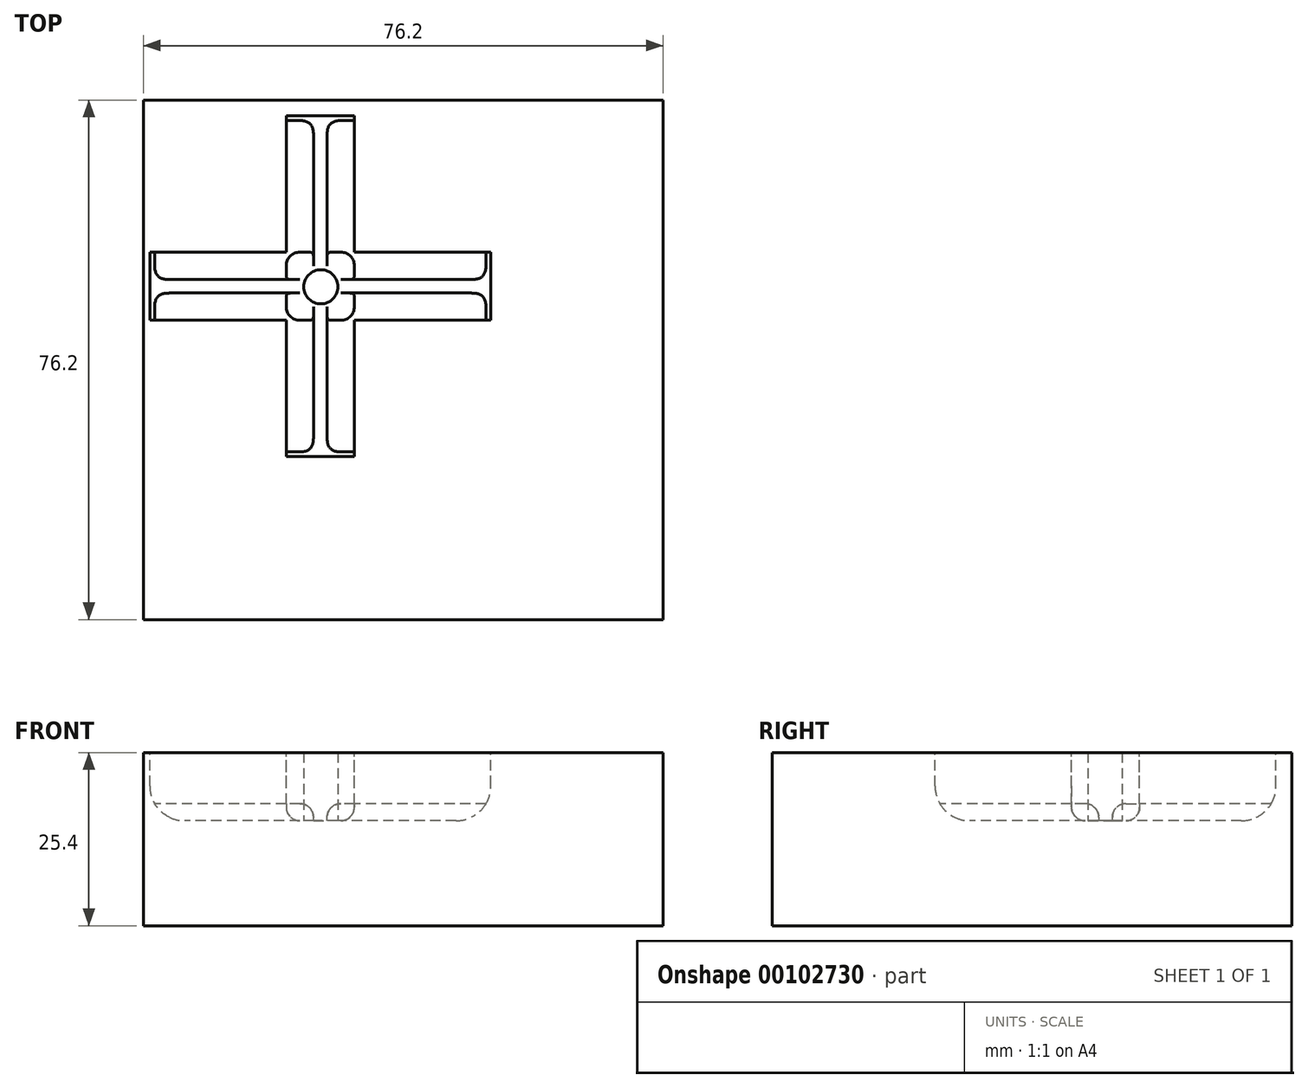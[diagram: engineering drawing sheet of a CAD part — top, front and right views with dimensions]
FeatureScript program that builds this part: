
annotation { "Feature Type Name" : "Feature", "Feature Type Description" : "" }
export const myFeature = defineFeature(function(context is Context, id is Id, definition is map)
    precondition{}
    {
        {
            var Q0;
            Q0=qCreatedBy(makeId("Top.planeOp"),FACE);
            var sketch = newSketch(context, id + "F0", { "sketchPlane" : qUnion([Q0])});
            skLineSegment(sketch, "E0.bottom", {"start": v(0, 0) * mm, "end": v(50.8, 0) * mm});
            skLineSegment(sketch, "E0.top", {"start": v(0, -50.8) * mm, "end": v(50.8, -50.8) * mm});
            skLineSegment(sketch, "E0.left", {"start": v(0, 0) * mm, "end": v(0, -50.8) * mm});
            skLineSegment(sketch, "E0.right", {"start": v(50.8, 0) * mm, "end": v(50.8, -50.8) * mm});
            skSolve(sketch);
        }
        {
            var Q0;
            Q0=makeQuery(id+"F0.imprint","IMPRINT",FACE,{"disambiguationData":[TD([[makeQuery(id+"F0.imprint","IMPRINT",EDGE,{"derivedFrom":sQuery(id+"F0.wireOp",EDGE,"E0.bottom")}),-1.0]])]});
            extrude(context, id + "F1", {"entities" : qUnion([Q0]), "depth" : 25.4 * mm});
        }
        {
            var Q0;
            Q0=makeQuery(id+"F1.opExtrude","SWEPT_FACE",FACE,{"disambiguationData":[OSD([sQuery(id+"F0.wireOp",EDGE,"E0.top")])]});
            extrude(context, id + "F2", {"entities" : qUnion([Q0]), "operationType" : NewBodyOperationType.ADD, "depth" : 25.4 * mm});
        }
        {
            var Q0;
            {var subQ0=sQuery(id+"F0.wireOp",EDGE,"E0.top");Q0=makeQuery(id+"F2.boolean.opBoolean","MERGE",FACE,{"derivedFrom":[makeQuery(id+"F1.opExtrude","CAP_FACE",FACE,{"disambiguationData":[OSD([sQuery(id+"F0.wireOp",EDGE,"E0.bottom"),subQ0,sQuery(id+"F0.wireOp",EDGE,"E0.left"),sQuery(id+"F0.wireOp",EDGE,"E0.right")])],"isStart":false}),makeQuery(id+"F2.opExtrude","SWEPT_FACE",FACE,{"disambiguationData":[OSD([subQ0]),TDD([makeQuery(id+"F1.opExtrude","CAP_EDGE",EDGE,{"disambiguationData":[OSD([subQ0])],"isStart":false})])]})]});}
            var sketch = newSketch(context, id + "F3", { "sketchPlane" : qUnion([Q0])});
            skPoint(sketch, "E1.startSnap0", {"position": v(25.4, 0) * mm});
            skLineSegment(sketch, "E2.0", {"start": v(20.93, -12.32) * mm, "end": v(20.93, -22.32) * mm});
            skLineSegment(sketch, "E3.0", {"start": v(30.93, -12.32) * mm, "end": v(30.93, -22.32) * mm});
            skLineSegment(sketch, "E4.0", {"start": v(40.93, -22.32) * mm, "end": v(30.93, -22.32) * mm});
            skLineSegment(sketch, "E5.0", {"start": v(20.93, -22.32) * mm, "end": v(10.93, -22.32) * mm});
            skLineSegment(sketch, "E6.0", {"start": v(20.93, -32.32) * mm, "end": v(10.93, -32.32) * mm});
            skLineSegment(sketch, "E7.0", {"start": v(40.93, -32.32) * mm, "end": v(30.93, -32.32) * mm});
            skLineSegment(sketch, "E8", {"start": v(10.93, -22.32) * mm, "end": v(10.93, -32.32) * mm});
            skLineSegment(sketch, "E9", {"start": v(40.93, -22.32) * mm, "end": v(40.93, -32.32) * mm});
            skLineSegment(sketch, "E10", {"start": v(30.93, -12.32) * mm, "end": v(20.93, -12.32) * mm});
            skLineSegment(sketch, "E11", {"start": v(20.93, -42.32) * mm, "end": v(30.93, -42.32) * mm});
            skPoint(sketch, "E12.orphan", {"position": v(25.4, -22.99) * mm});
            skPoint(sketch, "E13.orphan", {"position": v(25.93, -42.32) * mm});
            skLineSegment(sketch, "E14.trimOffspring", {"start": v(30.93, -32.32) * mm, "end": v(30.93, -42.32) * mm});
            skLineSegment(sketch, "E15.trimOffspring", {"start": v(20.93, -32.32) * mm, "end": v(20.93, -42.32) * mm});
            skSolve(sketch);
        }
        {
            var Q0;
            Q0=makeQuery(id+"F3.imprint","IMPRINT",FACE,{"disambiguationData":[TD([[makeQuery(id+"F3.imprint","IMPRINT",EDGE,{"derivedFrom":sQuery(id+"F3.wireOp",EDGE,"E2.0")}),1.0]])]});
            extrude(context, id + "F4", {"entities" : qUnion([Q0]), "operationType" : NewBodyOperationType.REMOVE, "oppositeDirection" : true, "depth" : 10 * mm});
        }
        {
            var Q0;
            Q0=makeQuery(id+"F4.boolean.opBoolean","COPY",FACE,{"derivedFrom":makeQuery(id+"F4.opExtrude","SWEPT_FACE",FACE,{"disambiguationData":[OSD([sQuery(id+"F3.wireOp",EDGE,"E8")])]})});
            extrude(context, id + "F5", {"entities" : qUnion([Q0]), "operationType" : NewBodyOperationType.REMOVE, "oppositeDirection" : true, "depth" : 10 * mm});
        }
        {
            var Q0;
            Q0=makeQuery(id+"F4.boolean.opBoolean","COPY",FACE,{"derivedFrom":makeQuery(id+"F4.opExtrude","SWEPT_FACE",FACE,{"disambiguationData":[OSD([sQuery(id+"F3.wireOp",EDGE,"E10")])]})});
            extrude(context, id + "F6", {"entities" : qUnion([Q0]), "operationType" : NewBodyOperationType.REMOVE, "oppositeDirection" : true, "depth" : 10 * mm});
        }
        {
            var Q0;
            {var subQ0=sQuery(id+"F0.wireOp",EDGE,"E0.right");Q0=makeQuery(id+"F2.boolean.opBoolean","MERGE",FACE,{"derivedFrom":[makeQuery(id+"F1.opExtrude","SWEPT_FACE",FACE,{"disambiguationData":[OSD([subQ0])]}),makeQuery(id+"F2.opExtrude","SWEPT_FACE",FACE,{"disambiguationData":[OSD([sQuery(id+"F0.wireOp",EDGE,"E0.top"),subQ0])]})]});}
            extrude(context, id + "F7", {"entities" : qUnion([Q0]), "operationType" : NewBodyOperationType.ADD, "depth" : 25.4 * mm});
        }
        {
            var Q0;
            Q0=makeQuery(id+"F4.boolean.opBoolean","COPY",FACE,{"derivedFrom":makeQuery(id+"F4.opExtrude","SWEPT_FACE",FACE,{"disambiguationData":[OSD([sQuery(id+"F3.wireOp",EDGE,"E9")])]})});
            extrude(context, id + "F8", {"entities" : qUnion([Q0]), "operationType" : NewBodyOperationType.REMOVE, "oppositeDirection" : true, "depth" : 10 * mm});
        }
        {
            var Q0;
            Q0=makeQuery(id+"F4.boolean.opBoolean","COPY",FACE,{"derivedFrom":makeQuery(id+"F4.opExtrude","SWEPT_FACE",FACE,{"disambiguationData":[OSD([sQuery(id+"F3.wireOp",EDGE,"E11")])]})});
            extrude(context, id + "F9", {"entities" : qUnion([Q0]), "operationType" : NewBodyOperationType.REMOVE, "oppositeDirection" : true, "depth" : 10 * mm});
        }
        {
            var Q0;
            {var subQ0=sQuery(id+"F3.wireOp",EDGE,"E11");var subQ1=sQuery(id+"F3.wireOp",EDGE,"E9");var subQ2=sQuery(id+"F3.wireOp",EDGE,"E10");var subQ3=sQuery(id+"F3.wireOp",EDGE,"E8");Q0=makeQuery(id+"F9.boolean.opBoolean","MERGE",FACE,{"derivedFrom":[makeQuery(id+"F8.boolean.opBoolean","MERGE",FACE,{"derivedFrom":[makeQuery(id+"F6.boolean.opBoolean","MERGE",FACE,{"derivedFrom":[makeQuery(id+"F5.boolean.opBoolean","MERGE",FACE,{"derivedFrom":[makeQuery(id+"F4.boolean.opBoolean","COPY",FACE,{"derivedFrom":makeQuery(id+"F4.opExtrude","CAP_FACE",FACE,{"disambiguationData":[OSD([sQuery(id+"F3.wireOp",EDGE,"E2.0"),sQuery(id+"F3.wireOp",EDGE,"E3.0"),sQuery(id+"F3.wireOp",EDGE,"E4.0"),sQuery(id+"F3.wireOp",EDGE,"E5.0"),sQuery(id+"F3.wireOp",EDGE,"E6.0"),sQuery(id+"F3.wireOp",EDGE,"E7.0"),subQ3,subQ1,subQ2,subQ0,sQuery(id+"F3.wireOp",EDGE,"E14.trimOffspring"),sQuery(id+"F3.wireOp",EDGE,"E15.trimOffspring")])],"isStart":false})}),makeQuery(id+"F5.opExtrude","SWEPT_FACE",FACE,{"disambiguationData":[OSD([subQ3]),TDD([makeQuery(id+"F4.boolean.opBoolean","COPY",EDGE,{"derivedFrom":makeQuery(id+"F4.opExtrude","CAP_EDGE",EDGE,{"disambiguationData":[OSD([subQ3])],"isStart":false})})])]})]}),makeQuery(id+"F6.opExtrude","SWEPT_FACE",FACE,{"disambiguationData":[OSD([subQ2]),TDD([makeQuery(id+"F4.boolean.opBoolean","COPY",EDGE,{"derivedFrom":makeQuery(id+"F4.opExtrude","CAP_EDGE",EDGE,{"disambiguationData":[OSD([subQ2])],"isStart":false})})])]})]}),makeQuery(id+"F8.opExtrude","SWEPT_FACE",FACE,{"disambiguationData":[OSD([subQ1]),TDD([makeQuery(id+"F4.boolean.opBoolean","COPY",EDGE,{"derivedFrom":makeQuery(id+"F4.opExtrude","CAP_EDGE",EDGE,{"disambiguationData":[OSD([subQ1])],"isStart":false})})])]})]}),makeQuery(id+"F9.opExtrude","SWEPT_FACE",FACE,{"disambiguationData":[OSD([subQ0]),TDD([makeQuery(id+"F4.boolean.opBoolean","COPY",EDGE,{"derivedFrom":makeQuery(id+"F4.opExtrude","CAP_EDGE",EDGE,{"disambiguationData":[OSD([subQ0])],"isStart":false})})])]})]});}
            var sketch = newSketch(context, id + "F10", { "sketchPlane" : qUnion([Q0])});
            skCircle(sketch, "E16", {"center": v(26.01, -27.4) * mm, "radius": 2.5 * mm});
            skSolve(sketch);
        }
        {
            var Q0;
            Q0=makeQuery(id+"F10.imprint","IMPRINT",FACE,{"disambiguationData":[TD([[makeQuery(id+"F10.imprint","IMPRINT",EDGE,{"derivedFrom":sQuery(id+"F10.wireOp",EDGE,"E16")}),1.0]])]});
            extrude(context, id + "F11", {"entities" : qUnion([Q0]), "operationType" : NewBodyOperationType.ADD, "depth" : 10 * mm});
        }
        {
            var Q0;
            {var subQ0=sQuery(id+"F3.wireOp",EDGE,"E11");var subQ1=sQuery(id+"F3.wireOp",EDGE,"E9");var subQ2=sQuery(id+"F3.wireOp",EDGE,"E10");var subQ3=sQuery(id+"F3.wireOp",EDGE,"E8");Q0=makeQuery(id+"F9.boolean.opBoolean","MERGE",FACE,{"derivedFrom":[makeQuery(id+"F8.boolean.opBoolean","MERGE",FACE,{"derivedFrom":[makeQuery(id+"F6.boolean.opBoolean","MERGE",FACE,{"derivedFrom":[makeQuery(id+"F5.boolean.opBoolean","MERGE",FACE,{"derivedFrom":[makeQuery(id+"F4.boolean.opBoolean","COPY",FACE,{"derivedFrom":makeQuery(id+"F4.opExtrude","CAP_FACE",FACE,{"disambiguationData":[OSD([sQuery(id+"F3.wireOp",EDGE,"E2.0"),sQuery(id+"F3.wireOp",EDGE,"E3.0"),sQuery(id+"F3.wireOp",EDGE,"E4.0"),sQuery(id+"F3.wireOp",EDGE,"E5.0"),sQuery(id+"F3.wireOp",EDGE,"E6.0"),sQuery(id+"F3.wireOp",EDGE,"E7.0"),subQ3,subQ1,subQ2,subQ0,sQuery(id+"F3.wireOp",EDGE,"E14.trimOffspring"),sQuery(id+"F3.wireOp",EDGE,"E15.trimOffspring")])],"isStart":false})}),makeQuery(id+"F5.opExtrude","SWEPT_FACE",FACE,{"disambiguationData":[OSD([subQ3]),TDD([makeQuery(id+"F4.boolean.opBoolean","COPY",EDGE,{"derivedFrom":makeQuery(id+"F4.opExtrude","CAP_EDGE",EDGE,{"disambiguationData":[OSD([subQ3])],"isStart":false})})])]})]}),makeQuery(id+"F6.opExtrude","SWEPT_FACE",FACE,{"disambiguationData":[OSD([subQ2]),TDD([makeQuery(id+"F4.boolean.opBoolean","COPY",EDGE,{"derivedFrom":makeQuery(id+"F4.opExtrude","CAP_EDGE",EDGE,{"disambiguationData":[OSD([subQ2])],"isStart":false})})])]})]}),makeQuery(id+"F8.opExtrude","SWEPT_FACE",FACE,{"disambiguationData":[OSD([subQ1]),TDD([makeQuery(id+"F4.boolean.opBoolean","COPY",EDGE,{"derivedFrom":makeQuery(id+"F4.opExtrude","CAP_EDGE",EDGE,{"disambiguationData":[OSD([subQ1])],"isStart":false})})])]})]}),makeQuery(id+"F9.opExtrude","SWEPT_FACE",FACE,{"disambiguationData":[OSD([subQ0]),TDD([makeQuery(id+"F4.boolean.opBoolean","COPY",EDGE,{"derivedFrom":makeQuery(id+"F4.opExtrude","CAP_EDGE",EDGE,{"disambiguationData":[OSD([subQ0])],"isStart":false})})])]})]});}
            var sketch = newSketch(context, id + "F12", { "sketchPlane" : qUnion([Q0])});
            skLineSegment(sketch, "E17.0", {"start": v(50.93, -26.32) * mm, "end": v(30.93, -26.32) * mm});
            skLineSegment(sketch, "E18.0", {"start": v(26.93, -2.32) * mm, "end": v(26.93, -22.32) * mm});
            skLineSegment(sketch, "E19.0", {"start": v(24.93, -2.32) * mm, "end": v(24.93, -22.32) * mm});
            skLineSegment(sketch, "E20.0", {"start": v(20.93, -26.32) * mm, "end": v(0.93, -26.32) * mm});
            skLineSegment(sketch, "E21.0", {"start": v(20.93, -28.32) * mm, "end": v(0.93, -28.32) * mm});
            skLineSegment(sketch, "E22.0", {"start": v(24.93, -32.32) * mm, "end": v(24.93, -52.32) * mm});
            skLineSegment(sketch, "E23.0", {"start": v(26.93, -32.32) * mm, "end": v(26.93, -52.32) * mm});
            skLineSegment(sketch, "E24.0", {"start": v(50.93, -28.32) * mm, "end": v(30.93, -28.32) * mm});
            skLineSegment(sketch, "E25", {"start": v(30.93, -32.32) * mm, "end": v(30.93, -28.32) * mm});
            skLineSegment(sketch, "E26", {"start": v(30.93, -26.32) * mm, "end": v(30.93, -22.32) * mm});
            skLineSegment(sketch, "E27", {"start": v(30.93, -22.32) * mm, "end": v(26.93, -22.32) * mm});
            skLineSegment(sketch, "E28", {"start": v(24.93, -22.32) * mm, "end": v(20.93, -22.32) * mm});
            skLineSegment(sketch, "E29", {"start": v(20.93, -26.32) * mm, "end": v(20.93, -22.32) * mm});
            skLineSegment(sketch, "E30", {"start": v(20.93, -28.32) * mm, "end": v(20.93, -32.32) * mm});
            skLineSegment(sketch, "E31", {"start": v(20.93, -32.32) * mm, "end": v(24.93, -32.32) * mm});
            skLineSegment(sketch, "E32", {"start": v(26.93, -32.32) * mm, "end": v(30.93, -32.32) * mm});
            skSolve(sketch);
        }
        {
            var Q0;
            {var subQ0=sQuery(id+"F12.wireOp",EDGE,"E24.0");Q0=makeQuery(id+"F12.imprint","IMPRINT",FACE,{"disambiguationData":[TD([[makeQuery(id+"F12.imprint","IMPRINT",EDGE,{"derivedFrom":subQ0}),1.0]])]});}
            var Q1;
            {var subQ0=sQuery(id+"F12.wireOp",EDGE,"E17.0");Q1=makeQuery(id+"F12.imprint","IMPRINT",FACE,{"disambiguationData":[TD([[makeQuery(id+"F12.imprint","IMPRINT",EDGE,{"derivedFrom":subQ0}),-1.0]])]});}
            var Q2;
            {var subQ0=sQuery(id+"F12.wireOp",EDGE,"E18.0");Q2=makeQuery(id+"F12.imprint","IMPRINT",FACE,{"disambiguationData":[TD([[makeQuery(id+"F12.imprint","IMPRINT",EDGE,{"derivedFrom":subQ0}),1.0]])]});}
            var Q3;
            {var subQ0=sQuery(id+"F12.wireOp",EDGE,"E19.0");Q3=makeQuery(id+"F12.imprint","IMPRINT",FACE,{"disambiguationData":[TD([[makeQuery(id+"F12.imprint","IMPRINT",EDGE,{"derivedFrom":subQ0}),-1.0]])]});}
            var Q4;
            {var subQ0=sQuery(id+"F12.wireOp",EDGE,"E20.0");Q4=makeQuery(id+"F12.imprint","IMPRINT",FACE,{"disambiguationData":[TD([[makeQuery(id+"F12.imprint","IMPRINT",EDGE,{"derivedFrom":subQ0}),-1.0]])]});}
            var Q5;
            {var subQ0=sQuery(id+"F12.wireOp",EDGE,"E21.0");Q5=makeQuery(id+"F12.imprint","IMPRINT",FACE,{"disambiguationData":[TD([[makeQuery(id+"F12.imprint","IMPRINT",EDGE,{"derivedFrom":subQ0}),1.0]])]});}
            var Q6;
            {var subQ0=sQuery(id+"F12.wireOp",EDGE,"E22.0");Q6=makeQuery(id+"F12.imprint","IMPRINT",FACE,{"disambiguationData":[TD([[makeQuery(id+"F12.imprint","IMPRINT",EDGE,{"derivedFrom":subQ0}),-1.0]])]});}
            var Q7;
            {var subQ0=sQuery(id+"F12.wireOp",EDGE,"E23.0");Q7=makeQuery(id+"F12.imprint","IMPRINT",FACE,{"disambiguationData":[TD([[makeQuery(id+"F12.imprint","IMPRINT",EDGE,{"derivedFrom":subQ0}),1.0]])]});}
            extrude(context, id + "F13", {"entities" : qUnion([Q0, Q1, Q2, Q3, Q4, Q5, Q6, Q7]), "operationType" : NewBodyOperationType.ADD, "depth" : 2.5 * mm});
        }
        {
            var Q0;
            Q0=makeQuery(id+"F13.opExtrude","CAP_EDGE",EDGE,{"disambiguationData":[OSD([sQuery(id+"F12.wireOp",EDGE,"E17.0")])],"isStart":false});
            var Q1;
            Q1=makeQuery(id+"F13.opExtrude","CAP_EDGE",EDGE,{"disambiguationData":[OSD([sQuery(id+"F12.wireOp",EDGE,"E24.0")])],"isStart":false});
            var Q2;
            Q2=makeQuery(id+"F13.opExtrude","CAP_EDGE",EDGE,{"disambiguationData":[OSD([sQuery(id+"F12.wireOp",EDGE,"E18.0")])],"isStart":false});
            var Q3;
            Q3=makeQuery(id+"F13.opExtrude","CAP_EDGE",EDGE,{"disambiguationData":[OSD([sQuery(id+"F12.wireOp",EDGE,"E19.0")])],"isStart":false});
            var Q4;
            Q4=makeQuery(id+"F13.opExtrude","CAP_EDGE",EDGE,{"disambiguationData":[OSD([sQuery(id+"F12.wireOp",EDGE,"E20.0")])],"isStart":false});
            var Q5;
            Q5=makeQuery(id+"F13.opExtrude","CAP_EDGE",EDGE,{"disambiguationData":[OSD([sQuery(id+"F12.wireOp",EDGE,"E23.0")])],"isStart":false});
            var Q6;
            Q6=makeQuery(id+"F13.opExtrude","CAP_EDGE",EDGE,{"disambiguationData":[OSD([sQuery(id+"F12.wireOp",EDGE,"E22.0")])],"isStart":false});
            var Q7;
            Q7=makeQuery(id+"F13.opExtrude","CAP_EDGE",EDGE,{"disambiguationData":[OSD([sQuery(id+"F12.wireOp",EDGE,"E21.0")])],"isStart":false});
            fillet(context, id + "F14", {"entities" : qUnion([Q0, Q1, Q2, Q3, Q4, Q5, Q6, Q7]), "radius" : 2 * mm, "tangentPropagation" : true, "allowEdgeOverflow" : false});
        }
        {
            var Q0;
            {var subQ0=sQuery(id+"F3.wireOp",EDGE,"E9");Q0=makeQuery(id+"F8.boolean.opBoolean","COPY",EDGE,{"derivedFrom":makeQuery(id+"F8.opExtrude","CAP_EDGE",EDGE,{"disambiguationData":[OSD([subQ0]),TDD([makeQuery(id+"F4.boolean.opBoolean","COPY",EDGE,{"derivedFrom":makeQuery(id+"F4.opExtrude","CAP_EDGE",EDGE,{"disambiguationData":[OSD([subQ0])],"isStart":false})})])],"isStart":false})});}
            var Q1;
            {var subQ0=sQuery(id+"F3.wireOp",EDGE,"E11");Q1=makeQuery(id+"F9.boolean.opBoolean","COPY",EDGE,{"derivedFrom":makeQuery(id+"F9.opExtrude","CAP_EDGE",EDGE,{"disambiguationData":[OSD([subQ0]),TDD([makeQuery(id+"F4.boolean.opBoolean","COPY",EDGE,{"derivedFrom":makeQuery(id+"F4.opExtrude","CAP_EDGE",EDGE,{"disambiguationData":[OSD([subQ0])],"isStart":false})})])],"isStart":false})});}
            var Q2;
            {var subQ0=sQuery(id+"F3.wireOp",EDGE,"E8");Q2=makeQuery(id+"F5.boolean.opBoolean","COPY",EDGE,{"derivedFrom":makeQuery(id+"F5.opExtrude","CAP_EDGE",EDGE,{"disambiguationData":[OSD([subQ0]),TDD([makeQuery(id+"F4.boolean.opBoolean","COPY",EDGE,{"derivedFrom":makeQuery(id+"F4.opExtrude","CAP_EDGE",EDGE,{"disambiguationData":[OSD([subQ0])],"isStart":false})})])],"isStart":false})});}
            var Q3;
            {var subQ0=sQuery(id+"F3.wireOp",EDGE,"E10");Q3=makeQuery(id+"F6.boolean.opBoolean","COPY",EDGE,{"derivedFrom":makeQuery(id+"F6.opExtrude","CAP_EDGE",EDGE,{"disambiguationData":[OSD([subQ0]),TDD([makeQuery(id+"F4.boolean.opBoolean","COPY",EDGE,{"derivedFrom":makeQuery(id+"F4.opExtrude","CAP_EDGE",EDGE,{"disambiguationData":[OSD([subQ0])],"isStart":false})})])],"isStart":false})});}
            fillet(context, id + "F15", {"entities" : qUnion([Q0, Q1, Q2, Q3]), "radius" : 5.08 * mm, "tangentPropagation" : true, "allowEdgeOverflow" : false});
        }
        {
            var Q0;
            {var subQ0=sQuery(id+"F12.wireOp",EDGE,"E32");var subQ1=sQuery(id+"F3.wireOp",EDGE,"E14.trimOffspring");var subQ2=sQuery(id+"F3.wireOp",EDGE,"E11");Q0=makeQuery(id+"F13.opExtrude","SWEPT_EDGE",EDGE,{"disambiguationData":[OSD([sQuery(id+"F3.wireOp",EDGE,"E7.0"),sQuery(id+"F3.wireOp",EDGE,"E9"),subQ2,subQ1,sQuery(id+"F12.wireOp",EDGE,"E25"),subQ0]),ownerDisambiguation([makeQuery(id+"F13.opExtrude","SWEPT_BODY",BODY,{"disambiguationData":[OSD([subQ2,subQ1,sQuery(id+"F12.wireOp",EDGE,"E23.0"),subQ0])]})])]});}
            var Q1;
            {var subQ0=sQuery(id+"F12.wireOp",EDGE,"E30");var subQ1=sQuery(id+"F3.wireOp",EDGE,"E8");var subQ2=sQuery(id+"F3.wireOp",EDGE,"E6.0");Q1=makeQuery(id+"F13.opExtrude","SWEPT_EDGE",EDGE,{"disambiguationData":[OSD([subQ2,subQ1,sQuery(id+"F3.wireOp",EDGE,"E11"),sQuery(id+"F3.wireOp",EDGE,"E15.trimOffspring"),subQ0,sQuery(id+"F12.wireOp",EDGE,"E31")]),ownerDisambiguation([makeQuery(id+"F13.opExtrude","SWEPT_BODY",BODY,{"disambiguationData":[OSD([subQ2,subQ1,sQuery(id+"F12.wireOp",EDGE,"E21.0"),subQ0])]})])]});}
            var Q2;
            {var subQ0=sQuery(id+"F12.wireOp",EDGE,"E28");var subQ1=sQuery(id+"F3.wireOp",EDGE,"E10");var subQ2=sQuery(id+"F3.wireOp",EDGE,"E2.0");Q2=makeQuery(id+"F13.opExtrude","SWEPT_EDGE",EDGE,{"disambiguationData":[OSD([subQ2,sQuery(id+"F3.wireOp",EDGE,"E5.0"),sQuery(id+"F3.wireOp",EDGE,"E8"),subQ1,subQ0,sQuery(id+"F12.wireOp",EDGE,"E29")]),ownerDisambiguation([makeQuery(id+"F13.opExtrude","SWEPT_BODY",BODY,{"disambiguationData":[OSD([subQ2,subQ1,sQuery(id+"F12.wireOp",EDGE,"E19.0"),subQ0])]})])]});}
            var Q3;
            {var subQ0=sQuery(id+"F12.wireOp",EDGE,"E26");var subQ1=sQuery(id+"F3.wireOp",EDGE,"E9");var subQ2=sQuery(id+"F3.wireOp",EDGE,"E4.0");Q3=makeQuery(id+"F13.opExtrude","SWEPT_EDGE",EDGE,{"disambiguationData":[OSD([sQuery(id+"F3.wireOp",EDGE,"E3.0"),subQ2,subQ1,sQuery(id+"F3.wireOp",EDGE,"E10"),subQ0,sQuery(id+"F12.wireOp",EDGE,"E27")]),ownerDisambiguation([makeQuery(id+"F13.opExtrude","SWEPT_BODY",BODY,{"disambiguationData":[OSD([subQ2,subQ1,sQuery(id+"F12.wireOp",EDGE,"E17.0"),subQ0])]})])]});}
            fillet(context, id + "F16", {"entities" : qUnion([Q0, Q1, Q2, Q3]), "radius" : 2 * mm, "tangentPropagation" : true, "allowEdgeOverflow" : false});
        }
        {
            var Q0;
            {var subQ0=sQuery(id+"F3.wireOp",EDGE,"E11");var subQ1=sQuery(id+"F3.wireOp",EDGE,"E9");var subQ2=sQuery(id+"F3.wireOp",EDGE,"E10");var subQ3=sQuery(id+"F3.wireOp",EDGE,"E8");var subQ4=sQuery(id+"F3.wireOp",EDGE,"E15.trimOffspring");var subQ5=sQuery(id+"F3.wireOp",EDGE,"E6.0");var subQ6=sQuery(id+"F12.wireOp",EDGE,"E30");Q0=makeQuery(id+"F16.opFillet","BLEND_EDGE",EDGE,{"blendedFrom":[makeQuery(id+"F13.opExtrude","SWEPT_EDGE",EDGE,{"disambiguationData":[OSD([subQ5,subQ3,subQ0,subQ4,subQ6,sQuery(id+"F12.wireOp",EDGE,"E31")]),ownerDisambiguation([makeQuery(id+"F13.opExtrude","SWEPT_BODY",BODY,{"disambiguationData":[OSD([subQ5,subQ3,sQuery(id+"F12.wireOp",EDGE,"E21.0"),subQ6])]})])]}),makeQuery(id+"F9.boolean.opBoolean","MERGE",FACE,{"derivedFrom":[makeQuery(id+"F8.boolean.opBoolean","MERGE",FACE,{"derivedFrom":[makeQuery(id+"F6.boolean.opBoolean","MERGE",FACE,{"derivedFrom":[makeQuery(id+"F5.boolean.opBoolean","MERGE",FACE,{"derivedFrom":[makeQuery(id+"F4.boolean.opBoolean","COPY",FACE,{"derivedFrom":makeQuery(id+"F4.opExtrude","CAP_FACE",FACE,{"disambiguationData":[OSD([sQuery(id+"F3.wireOp",EDGE,"E2.0"),sQuery(id+"F3.wireOp",EDGE,"E3.0"),sQuery(id+"F3.wireOp",EDGE,"E4.0"),sQuery(id+"F3.wireOp",EDGE,"E5.0"),subQ5,sQuery(id+"F3.wireOp",EDGE,"E7.0"),subQ3,subQ1,subQ2,subQ0,sQuery(id+"F3.wireOp",EDGE,"E14.trimOffspring"),subQ4])],"isStart":false})}),makeQuery(id+"F5.opExtrude","SWEPT_FACE",FACE,{"disambiguationData":[OSD([subQ3]),TDD([makeQuery(id+"F4.boolean.opBoolean","COPY",EDGE,{"derivedFrom":makeQuery(id+"F4.opExtrude","CAP_EDGE",EDGE,{"disambiguationData":[OSD([subQ3])],"isStart":false})})])]})]}),makeQuery(id+"F6.opExtrude","SWEPT_FACE",FACE,{"disambiguationData":[OSD([subQ2]),TDD([makeQuery(id+"F4.boolean.opBoolean","COPY",EDGE,{"derivedFrom":makeQuery(id+"F4.opExtrude","CAP_EDGE",EDGE,{"disambiguationData":[OSD([subQ2])],"isStart":false})})])]})]}),makeQuery(id+"F8.opExtrude","SWEPT_FACE",FACE,{"disambiguationData":[OSD([subQ1]),TDD([makeQuery(id+"F4.boolean.opBoolean","COPY",EDGE,{"derivedFrom":makeQuery(id+"F4.opExtrude","CAP_EDGE",EDGE,{"disambiguationData":[OSD([subQ1])],"isStart":false})})])]})]}),makeQuery(id+"F9.opExtrude","SWEPT_FACE",FACE,{"disambiguationData":[OSD([subQ0]),TDD([makeQuery(id+"F4.boolean.opBoolean","COPY",EDGE,{"derivedFrom":makeQuery(id+"F4.opExtrude","CAP_EDGE",EDGE,{"disambiguationData":[OSD([subQ0])],"isStart":false})})])]})]})],"blendedInto":[makeQuery(id+"F9.boolean.opBoolean","MERGE",FACE,{"derivedFrom":[makeQuery(id+"F8.boolean.opBoolean","MERGE",FACE,{"derivedFrom":[makeQuery(id+"F6.boolean.opBoolean","MERGE",FACE,{"derivedFrom":[makeQuery(id+"F5.boolean.opBoolean","MERGE",FACE,{"derivedFrom":[makeQuery(id+"F4.boolean.opBoolean","COPY",FACE,{"derivedFrom":makeQuery(id+"F4.opExtrude","CAP_FACE",FACE,{"disambiguationData":[OSD([sQuery(id+"F3.wireOp",EDGE,"E2.0"),sQuery(id+"F3.wireOp",EDGE,"E3.0"),sQuery(id+"F3.wireOp",EDGE,"E4.0"),sQuery(id+"F3.wireOp",EDGE,"E5.0"),subQ5,sQuery(id+"F3.wireOp",EDGE,"E7.0"),subQ3,subQ1,subQ2,subQ0,sQuery(id+"F3.wireOp",EDGE,"E14.trimOffspring"),subQ4])],"isStart":false})}),makeQuery(id+"F5.opExtrude","SWEPT_FACE",FACE,{"disambiguationData":[OSD([subQ3]),TDD([makeQuery(id+"F4.boolean.opBoolean","COPY",EDGE,{"derivedFrom":makeQuery(id+"F4.opExtrude","CAP_EDGE",EDGE,{"disambiguationData":[OSD([subQ3])],"isStart":false})})])]})]}),makeQuery(id+"F6.opExtrude","SWEPT_FACE",FACE,{"disambiguationData":[OSD([subQ2]),TDD([makeQuery(id+"F4.boolean.opBoolean","COPY",EDGE,{"derivedFrom":makeQuery(id+"F4.opExtrude","CAP_EDGE",EDGE,{"disambiguationData":[OSD([subQ2])],"isStart":false})})])]})]}),makeQuery(id+"F8.opExtrude","SWEPT_FACE",FACE,{"disambiguationData":[OSD([subQ1]),TDD([makeQuery(id+"F4.boolean.opBoolean","COPY",EDGE,{"derivedFrom":makeQuery(id+"F4.opExtrude","CAP_EDGE",EDGE,{"disambiguationData":[OSD([subQ1])],"isStart":false})})])]})]}),makeQuery(id+"F9.opExtrude","SWEPT_FACE",FACE,{"disambiguationData":[OSD([subQ0]),TDD([makeQuery(id+"F4.boolean.opBoolean","COPY",EDGE,{"derivedFrom":makeQuery(id+"F4.opExtrude","CAP_EDGE",EDGE,{"disambiguationData":[OSD([subQ0])],"isStart":false})})])]})]})]});}
            var Q1;
            {var subQ0=sQuery(id+"F3.wireOp",EDGE,"E11");var subQ1=sQuery(id+"F3.wireOp",EDGE,"E9");var subQ2=sQuery(id+"F3.wireOp",EDGE,"E10");var subQ3=sQuery(id+"F3.wireOp",EDGE,"E8");var subQ4=sQuery(id+"F3.wireOp",EDGE,"E14.trimOffspring");var subQ5=sQuery(id+"F3.wireOp",EDGE,"E7.0");var subQ6=sQuery(id+"F12.wireOp",EDGE,"E32");Q1=makeQuery(id+"F16.opFillet","BLEND_EDGE",EDGE,{"blendedFrom":[makeQuery(id+"F13.opExtrude","SWEPT_EDGE",EDGE,{"disambiguationData":[OSD([subQ5,subQ1,subQ0,subQ4,sQuery(id+"F12.wireOp",EDGE,"E25"),subQ6]),ownerDisambiguation([makeQuery(id+"F13.opExtrude","SWEPT_BODY",BODY,{"disambiguationData":[OSD([subQ0,subQ4,sQuery(id+"F12.wireOp",EDGE,"E23.0"),subQ6])]})])]}),makeQuery(id+"F9.boolean.opBoolean","MERGE",FACE,{"derivedFrom":[makeQuery(id+"F8.boolean.opBoolean","MERGE",FACE,{"derivedFrom":[makeQuery(id+"F6.boolean.opBoolean","MERGE",FACE,{"derivedFrom":[makeQuery(id+"F5.boolean.opBoolean","MERGE",FACE,{"derivedFrom":[makeQuery(id+"F4.boolean.opBoolean","COPY",FACE,{"derivedFrom":makeQuery(id+"F4.opExtrude","CAP_FACE",FACE,{"disambiguationData":[OSD([sQuery(id+"F3.wireOp",EDGE,"E2.0"),sQuery(id+"F3.wireOp",EDGE,"E3.0"),sQuery(id+"F3.wireOp",EDGE,"E4.0"),sQuery(id+"F3.wireOp",EDGE,"E5.0"),sQuery(id+"F3.wireOp",EDGE,"E6.0"),subQ5,subQ3,subQ1,subQ2,subQ0,subQ4,sQuery(id+"F3.wireOp",EDGE,"E15.trimOffspring")])],"isStart":false})}),makeQuery(id+"F5.opExtrude","SWEPT_FACE",FACE,{"disambiguationData":[OSD([subQ3]),TDD([makeQuery(id+"F4.boolean.opBoolean","COPY",EDGE,{"derivedFrom":makeQuery(id+"F4.opExtrude","CAP_EDGE",EDGE,{"disambiguationData":[OSD([subQ3])],"isStart":false})})])]})]}),makeQuery(id+"F6.opExtrude","SWEPT_FACE",FACE,{"disambiguationData":[OSD([subQ2]),TDD([makeQuery(id+"F4.boolean.opBoolean","COPY",EDGE,{"derivedFrom":makeQuery(id+"F4.opExtrude","CAP_EDGE",EDGE,{"disambiguationData":[OSD([subQ2])],"isStart":false})})])]})]}),makeQuery(id+"F8.opExtrude","SWEPT_FACE",FACE,{"disambiguationData":[OSD([subQ1]),TDD([makeQuery(id+"F4.boolean.opBoolean","COPY",EDGE,{"derivedFrom":makeQuery(id+"F4.opExtrude","CAP_EDGE",EDGE,{"disambiguationData":[OSD([subQ1])],"isStart":false})})])]})]}),makeQuery(id+"F9.opExtrude","SWEPT_FACE",FACE,{"disambiguationData":[OSD([subQ0]),TDD([makeQuery(id+"F4.boolean.opBoolean","COPY",EDGE,{"derivedFrom":makeQuery(id+"F4.opExtrude","CAP_EDGE",EDGE,{"disambiguationData":[OSD([subQ0])],"isStart":false})})])]})]})],"blendedInto":[makeQuery(id+"F9.boolean.opBoolean","MERGE",FACE,{"derivedFrom":[makeQuery(id+"F8.boolean.opBoolean","MERGE",FACE,{"derivedFrom":[makeQuery(id+"F6.boolean.opBoolean","MERGE",FACE,{"derivedFrom":[makeQuery(id+"F5.boolean.opBoolean","MERGE",FACE,{"derivedFrom":[makeQuery(id+"F4.boolean.opBoolean","COPY",FACE,{"derivedFrom":makeQuery(id+"F4.opExtrude","CAP_FACE",FACE,{"disambiguationData":[OSD([sQuery(id+"F3.wireOp",EDGE,"E2.0"),sQuery(id+"F3.wireOp",EDGE,"E3.0"),sQuery(id+"F3.wireOp",EDGE,"E4.0"),sQuery(id+"F3.wireOp",EDGE,"E5.0"),sQuery(id+"F3.wireOp",EDGE,"E6.0"),subQ5,subQ3,subQ1,subQ2,subQ0,subQ4,sQuery(id+"F3.wireOp",EDGE,"E15.trimOffspring")])],"isStart":false})}),makeQuery(id+"F5.opExtrude","SWEPT_FACE",FACE,{"disambiguationData":[OSD([subQ3]),TDD([makeQuery(id+"F4.boolean.opBoolean","COPY",EDGE,{"derivedFrom":makeQuery(id+"F4.opExtrude","CAP_EDGE",EDGE,{"disambiguationData":[OSD([subQ3])],"isStart":false})})])]})]}),makeQuery(id+"F6.opExtrude","SWEPT_FACE",FACE,{"disambiguationData":[OSD([subQ2]),TDD([makeQuery(id+"F4.boolean.opBoolean","COPY",EDGE,{"derivedFrom":makeQuery(id+"F4.opExtrude","CAP_EDGE",EDGE,{"disambiguationData":[OSD([subQ2])],"isStart":false})})])]})]}),makeQuery(id+"F8.opExtrude","SWEPT_FACE",FACE,{"disambiguationData":[OSD([subQ1]),TDD([makeQuery(id+"F4.boolean.opBoolean","COPY",EDGE,{"derivedFrom":makeQuery(id+"F4.opExtrude","CAP_EDGE",EDGE,{"disambiguationData":[OSD([subQ1])],"isStart":false})})])]})]}),makeQuery(id+"F9.opExtrude","SWEPT_FACE",FACE,{"disambiguationData":[OSD([subQ0]),TDD([makeQuery(id+"F4.boolean.opBoolean","COPY",EDGE,{"derivedFrom":makeQuery(id+"F4.opExtrude","CAP_EDGE",EDGE,{"disambiguationData":[OSD([subQ0])],"isStart":false})})])]})]})]});}
            var Q2;
            {var subQ0=sQuery(id+"F3.wireOp",EDGE,"E11");var subQ1=sQuery(id+"F3.wireOp",EDGE,"E9");var subQ2=sQuery(id+"F3.wireOp",EDGE,"E10");var subQ3=sQuery(id+"F3.wireOp",EDGE,"E8");var subQ4=sQuery(id+"F3.wireOp",EDGE,"E4.0");var subQ5=sQuery(id+"F3.wireOp",EDGE,"E3.0");var subQ6=sQuery(id+"F12.wireOp",EDGE,"E26");Q2=makeQuery(id+"F16.opFillet","BLEND_EDGE",EDGE,{"blendedFrom":[makeQuery(id+"F13.opExtrude","SWEPT_EDGE",EDGE,{"disambiguationData":[OSD([subQ5,subQ4,subQ1,subQ2,subQ6,sQuery(id+"F12.wireOp",EDGE,"E27")]),ownerDisambiguation([makeQuery(id+"F13.opExtrude","SWEPT_BODY",BODY,{"disambiguationData":[OSD([subQ4,subQ1,sQuery(id+"F12.wireOp",EDGE,"E17.0"),subQ6])]})])]}),makeQuery(id+"F9.boolean.opBoolean","MERGE",FACE,{"derivedFrom":[makeQuery(id+"F8.boolean.opBoolean","MERGE",FACE,{"derivedFrom":[makeQuery(id+"F6.boolean.opBoolean","MERGE",FACE,{"derivedFrom":[makeQuery(id+"F5.boolean.opBoolean","MERGE",FACE,{"derivedFrom":[makeQuery(id+"F4.boolean.opBoolean","COPY",FACE,{"derivedFrom":makeQuery(id+"F4.opExtrude","CAP_FACE",FACE,{"disambiguationData":[OSD([sQuery(id+"F3.wireOp",EDGE,"E2.0"),subQ5,subQ4,sQuery(id+"F3.wireOp",EDGE,"E5.0"),sQuery(id+"F3.wireOp",EDGE,"E6.0"),sQuery(id+"F3.wireOp",EDGE,"E7.0"),subQ3,subQ1,subQ2,subQ0,sQuery(id+"F3.wireOp",EDGE,"E14.trimOffspring"),sQuery(id+"F3.wireOp",EDGE,"E15.trimOffspring")])],"isStart":false})}),makeQuery(id+"F5.opExtrude","SWEPT_FACE",FACE,{"disambiguationData":[OSD([subQ3]),TDD([makeQuery(id+"F4.boolean.opBoolean","COPY",EDGE,{"derivedFrom":makeQuery(id+"F4.opExtrude","CAP_EDGE",EDGE,{"disambiguationData":[OSD([subQ3])],"isStart":false})})])]})]}),makeQuery(id+"F6.opExtrude","SWEPT_FACE",FACE,{"disambiguationData":[OSD([subQ2]),TDD([makeQuery(id+"F4.boolean.opBoolean","COPY",EDGE,{"derivedFrom":makeQuery(id+"F4.opExtrude","CAP_EDGE",EDGE,{"disambiguationData":[OSD([subQ2])],"isStart":false})})])]})]}),makeQuery(id+"F8.opExtrude","SWEPT_FACE",FACE,{"disambiguationData":[OSD([subQ1]),TDD([makeQuery(id+"F4.boolean.opBoolean","COPY",EDGE,{"derivedFrom":makeQuery(id+"F4.opExtrude","CAP_EDGE",EDGE,{"disambiguationData":[OSD([subQ1])],"isStart":false})})])]})]}),makeQuery(id+"F9.opExtrude","SWEPT_FACE",FACE,{"disambiguationData":[OSD([subQ0]),TDD([makeQuery(id+"F4.boolean.opBoolean","COPY",EDGE,{"derivedFrom":makeQuery(id+"F4.opExtrude","CAP_EDGE",EDGE,{"disambiguationData":[OSD([subQ0])],"isStart":false})})])]})]})],"blendedInto":[makeQuery(id+"F9.boolean.opBoolean","MERGE",FACE,{"derivedFrom":[makeQuery(id+"F8.boolean.opBoolean","MERGE",FACE,{"derivedFrom":[makeQuery(id+"F6.boolean.opBoolean","MERGE",FACE,{"derivedFrom":[makeQuery(id+"F5.boolean.opBoolean","MERGE",FACE,{"derivedFrom":[makeQuery(id+"F4.boolean.opBoolean","COPY",FACE,{"derivedFrom":makeQuery(id+"F4.opExtrude","CAP_FACE",FACE,{"disambiguationData":[OSD([sQuery(id+"F3.wireOp",EDGE,"E2.0"),subQ5,subQ4,sQuery(id+"F3.wireOp",EDGE,"E5.0"),sQuery(id+"F3.wireOp",EDGE,"E6.0"),sQuery(id+"F3.wireOp",EDGE,"E7.0"),subQ3,subQ1,subQ2,subQ0,sQuery(id+"F3.wireOp",EDGE,"E14.trimOffspring"),sQuery(id+"F3.wireOp",EDGE,"E15.trimOffspring")])],"isStart":false})}),makeQuery(id+"F5.opExtrude","SWEPT_FACE",FACE,{"disambiguationData":[OSD([subQ3]),TDD([makeQuery(id+"F4.boolean.opBoolean","COPY",EDGE,{"derivedFrom":makeQuery(id+"F4.opExtrude","CAP_EDGE",EDGE,{"disambiguationData":[OSD([subQ3])],"isStart":false})})])]})]}),makeQuery(id+"F6.opExtrude","SWEPT_FACE",FACE,{"disambiguationData":[OSD([subQ2]),TDD([makeQuery(id+"F4.boolean.opBoolean","COPY",EDGE,{"derivedFrom":makeQuery(id+"F4.opExtrude","CAP_EDGE",EDGE,{"disambiguationData":[OSD([subQ2])],"isStart":false})})])]})]}),makeQuery(id+"F8.opExtrude","SWEPT_FACE",FACE,{"disambiguationData":[OSD([subQ1]),TDD([makeQuery(id+"F4.boolean.opBoolean","COPY",EDGE,{"derivedFrom":makeQuery(id+"F4.opExtrude","CAP_EDGE",EDGE,{"disambiguationData":[OSD([subQ1])],"isStart":false})})])]})]}),makeQuery(id+"F9.opExtrude","SWEPT_FACE",FACE,{"disambiguationData":[OSD([subQ0]),TDD([makeQuery(id+"F4.boolean.opBoolean","COPY",EDGE,{"derivedFrom":makeQuery(id+"F4.opExtrude","CAP_EDGE",EDGE,{"disambiguationData":[OSD([subQ0])],"isStart":false})})])]})]})]});}
            var Q3;
            {var subQ0=sQuery(id+"F3.wireOp",EDGE,"E11");var subQ1=sQuery(id+"F3.wireOp",EDGE,"E9");var subQ2=sQuery(id+"F3.wireOp",EDGE,"E10");var subQ3=sQuery(id+"F3.wireOp",EDGE,"E8");var subQ4=sQuery(id+"F3.wireOp",EDGE,"E5.0");var subQ5=sQuery(id+"F3.wireOp",EDGE,"E2.0");var subQ6=sQuery(id+"F12.wireOp",EDGE,"E28");Q3=makeQuery(id+"F16.opFillet","BLEND_EDGE",EDGE,{"blendedFrom":[makeQuery(id+"F13.opExtrude","SWEPT_EDGE",EDGE,{"disambiguationData":[OSD([subQ5,subQ4,subQ3,subQ2,subQ6,sQuery(id+"F12.wireOp",EDGE,"E29")]),ownerDisambiguation([makeQuery(id+"F13.opExtrude","SWEPT_BODY",BODY,{"disambiguationData":[OSD([subQ5,subQ2,sQuery(id+"F12.wireOp",EDGE,"E19.0"),subQ6])]})])]}),makeQuery(id+"F9.boolean.opBoolean","MERGE",FACE,{"derivedFrom":[makeQuery(id+"F8.boolean.opBoolean","MERGE",FACE,{"derivedFrom":[makeQuery(id+"F6.boolean.opBoolean","MERGE",FACE,{"derivedFrom":[makeQuery(id+"F5.boolean.opBoolean","MERGE",FACE,{"derivedFrom":[makeQuery(id+"F4.boolean.opBoolean","COPY",FACE,{"derivedFrom":makeQuery(id+"F4.opExtrude","CAP_FACE",FACE,{"disambiguationData":[OSD([subQ5,sQuery(id+"F3.wireOp",EDGE,"E3.0"),sQuery(id+"F3.wireOp",EDGE,"E4.0"),subQ4,sQuery(id+"F3.wireOp",EDGE,"E6.0"),sQuery(id+"F3.wireOp",EDGE,"E7.0"),subQ3,subQ1,subQ2,subQ0,sQuery(id+"F3.wireOp",EDGE,"E14.trimOffspring"),sQuery(id+"F3.wireOp",EDGE,"E15.trimOffspring")])],"isStart":false})}),makeQuery(id+"F5.opExtrude","SWEPT_FACE",FACE,{"disambiguationData":[OSD([subQ3]),TDD([makeQuery(id+"F4.boolean.opBoolean","COPY",EDGE,{"derivedFrom":makeQuery(id+"F4.opExtrude","CAP_EDGE",EDGE,{"disambiguationData":[OSD([subQ3])],"isStart":false})})])]})]}),makeQuery(id+"F6.opExtrude","SWEPT_FACE",FACE,{"disambiguationData":[OSD([subQ2]),TDD([makeQuery(id+"F4.boolean.opBoolean","COPY",EDGE,{"derivedFrom":makeQuery(id+"F4.opExtrude","CAP_EDGE",EDGE,{"disambiguationData":[OSD([subQ2])],"isStart":false})})])]})]}),makeQuery(id+"F8.opExtrude","SWEPT_FACE",FACE,{"disambiguationData":[OSD([subQ1]),TDD([makeQuery(id+"F4.boolean.opBoolean","COPY",EDGE,{"derivedFrom":makeQuery(id+"F4.opExtrude","CAP_EDGE",EDGE,{"disambiguationData":[OSD([subQ1])],"isStart":false})})])]})]}),makeQuery(id+"F9.opExtrude","SWEPT_FACE",FACE,{"disambiguationData":[OSD([subQ0]),TDD([makeQuery(id+"F4.boolean.opBoolean","COPY",EDGE,{"derivedFrom":makeQuery(id+"F4.opExtrude","CAP_EDGE",EDGE,{"disambiguationData":[OSD([subQ0])],"isStart":false})})])]})]})],"blendedInto":[makeQuery(id+"F9.boolean.opBoolean","MERGE",FACE,{"derivedFrom":[makeQuery(id+"F8.boolean.opBoolean","MERGE",FACE,{"derivedFrom":[makeQuery(id+"F6.boolean.opBoolean","MERGE",FACE,{"derivedFrom":[makeQuery(id+"F5.boolean.opBoolean","MERGE",FACE,{"derivedFrom":[makeQuery(id+"F4.boolean.opBoolean","COPY",FACE,{"derivedFrom":makeQuery(id+"F4.opExtrude","CAP_FACE",FACE,{"disambiguationData":[OSD([subQ5,sQuery(id+"F3.wireOp",EDGE,"E3.0"),sQuery(id+"F3.wireOp",EDGE,"E4.0"),subQ4,sQuery(id+"F3.wireOp",EDGE,"E6.0"),sQuery(id+"F3.wireOp",EDGE,"E7.0"),subQ3,subQ1,subQ2,subQ0,sQuery(id+"F3.wireOp",EDGE,"E14.trimOffspring"),sQuery(id+"F3.wireOp",EDGE,"E15.trimOffspring")])],"isStart":false})}),makeQuery(id+"F5.opExtrude","SWEPT_FACE",FACE,{"disambiguationData":[OSD([subQ3]),TDD([makeQuery(id+"F4.boolean.opBoolean","COPY",EDGE,{"derivedFrom":makeQuery(id+"F4.opExtrude","CAP_EDGE",EDGE,{"disambiguationData":[OSD([subQ3])],"isStart":false})})])]})]}),makeQuery(id+"F6.opExtrude","SWEPT_FACE",FACE,{"disambiguationData":[OSD([subQ2]),TDD([makeQuery(id+"F4.boolean.opBoolean","COPY",EDGE,{"derivedFrom":makeQuery(id+"F4.opExtrude","CAP_EDGE",EDGE,{"disambiguationData":[OSD([subQ2])],"isStart":false})})])]})]}),makeQuery(id+"F8.opExtrude","SWEPT_FACE",FACE,{"disambiguationData":[OSD([subQ1]),TDD([makeQuery(id+"F4.boolean.opBoolean","COPY",EDGE,{"derivedFrom":makeQuery(id+"F4.opExtrude","CAP_EDGE",EDGE,{"disambiguationData":[OSD([subQ1])],"isStart":false})})])]})]}),makeQuery(id+"F9.opExtrude","SWEPT_FACE",FACE,{"disambiguationData":[OSD([subQ0]),TDD([makeQuery(id+"F4.boolean.opBoolean","COPY",EDGE,{"derivedFrom":makeQuery(id+"F4.opExtrude","CAP_EDGE",EDGE,{"disambiguationData":[OSD([subQ0])],"isStart":false})})])]})]})]});}
            fillet(context, id + "F17", {"entities" : qUnion([Q0, Q1, Q2, Q3]), "radius" : 2 * mm, "tangentPropagation" : true, "allowEdgeOverflow" : false});
        }
    });
